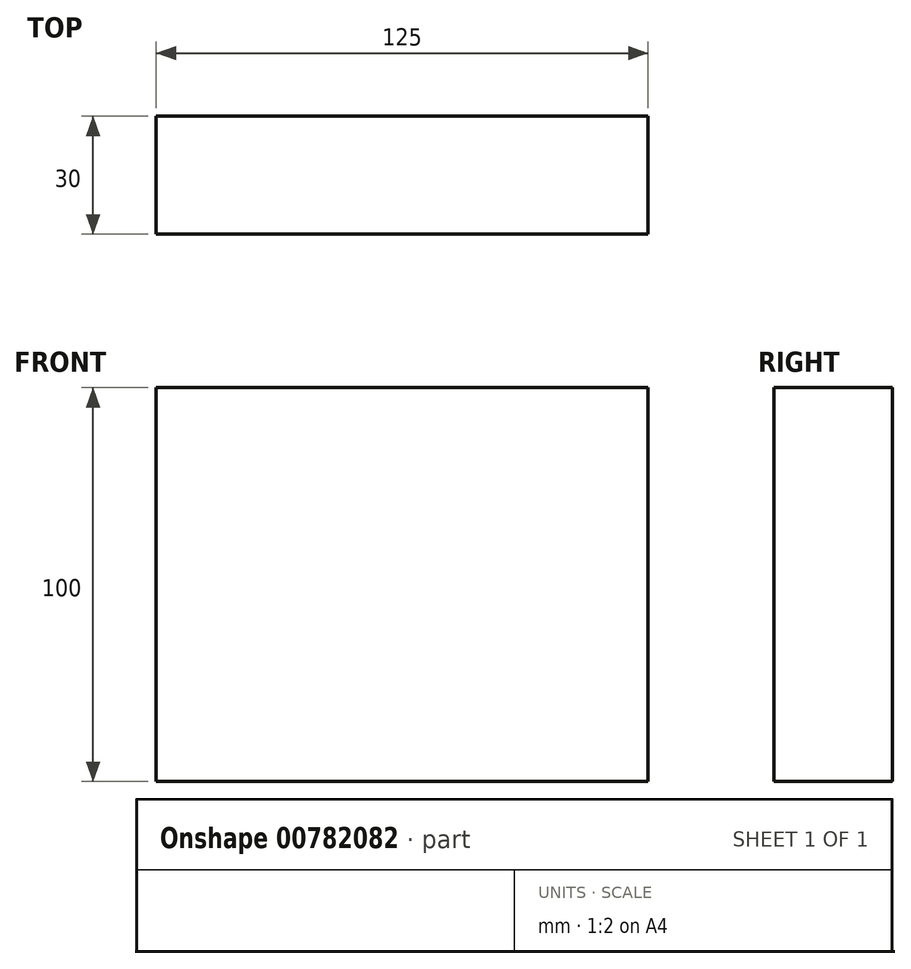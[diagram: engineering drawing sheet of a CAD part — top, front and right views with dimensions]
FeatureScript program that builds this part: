
annotation { "Feature Type Name" : "Feature", "Feature Type Description" : "" }
export const myFeature = defineFeature(function(context is Context, id is Id, definition is map)
    precondition{}
    {
        {
            var Q0;
            Q0=qCreatedBy(makeId("Top.planeOp"),FACE);
            var sketch = newSketch(context, id + "F0", { "sketchPlane" : qUnion([Q0])});
            skLineSegment(sketch, "E0.bottom", {"start": v(62.5, 15) * mm, "end": v(-62.5, 15) * mm});
            skLineSegment(sketch, "E0.top", {"start": v(62.5, -15) * mm, "end": v(-62.5, -15) * mm});
            skLineSegment(sketch, "E0.left", {"start": v(62.5, 15) * mm, "end": v(62.5, -15) * mm});
            skLineSegment(sketch, "E0.right", {"start": v(-62.5, 15) * mm, "end": v(-62.5, -15) * mm});
            skPoint(sketch, "E0.middle", {"position": v(0, 0) * mm});
            skSolve(sketch);
        }
        {
            var Q0;
            Q0=makeQuery(id+"F0.imprint","IMPRINT",FACE,{"disambiguationData":[TD([[makeQuery(id+"F0.imprint","IMPRINT",EDGE,{"derivedFrom":sQuery(id+"F0.wireOp",EDGE,"E0.bottom")}),1.0]])]});
            extrude(context, id + "F1", {"entities" : qUnion([Q0]), "depth" : 100 * mm, "offsetDistance" : 25 * mm});
        }
    });
